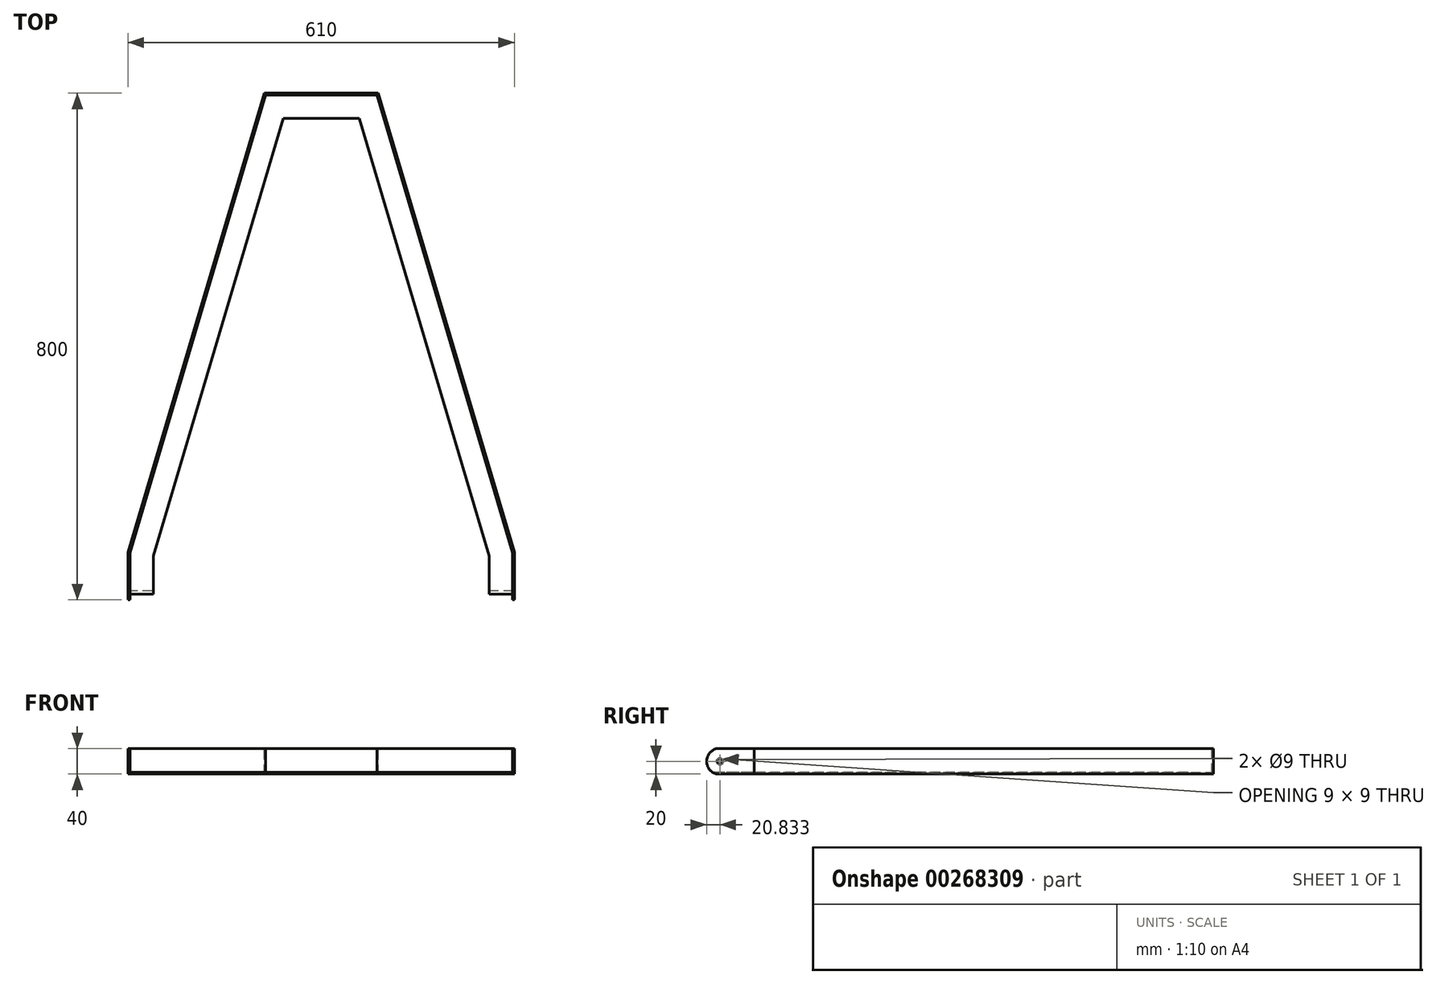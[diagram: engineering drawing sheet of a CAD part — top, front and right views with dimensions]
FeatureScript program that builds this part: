
annotation { "Feature Type Name" : "Feature", "Feature Type Description" : "" }
export const myFeature = defineFeature(function(context is Context, id is Id, definition is map)
    precondition{}
    {
        {
            var Q0;
            Q0=qCreatedBy(makeId("Top.planeOp"),FACE);
            var sketch = newSketch(context, id + "F0", { "sketchPlane" : qUnion([Q0])});
            skLineSegment(sketch, "E0", {"start": v(305, 0) * mm, "end": v(305, 75) * mm});
            skLineSegment(sketch, "E1", {"start": v(305, 75) * mm, "end": v(90, 800) * mm});
            skLineSegment(sketch, "E2", {"start": v(90, 800) * mm, "end": v(0, 800) * mm});
            skLineSegment(sketch, "E3.MirrorCS", {"start": v(-90, 800) * mm, "end": v(0, 800) * mm});
            skLineSegment(sketch, "E4.MirrorCS", {"start": v(-305, 75) * mm, "end": v(-90, 800) * mm});
            skLineSegment(sketch, "E5.MirrorCS", {"start": v(-305, 0) * mm, "end": v(-305, 75) * mm});
            skSolve(sketch);
        }
        {
            var Q0;
            Q0=qCreatedBy(makeId("Front.planeOp"),FACE);
            var sketch = newSketch(context, id + "F1", { "sketchPlane" : qUnion([Q0])});
            skLineSegment(sketch, "E6", {"start": v(305, 0) * mm, "end": v(305, 40) * mm});
            skLineSegment(sketch, "E7", {"start": v(305, 40) * mm, "end": v(302, 40) * mm});
            skLineSegment(sketch, "E8", {"start": v(302, 40) * mm, "end": v(302, 3) * mm});
            skLineSegment(sketch, "E9", {"start": v(302, 3) * mm, "end": v(265, 3) * mm});
            skLineSegment(sketch, "E10", {"start": v(265, 3) * mm, "end": v(265, 0) * mm});
            skLineSegment(sketch, "E11", {"start": v(265, 0) * mm, "end": v(305, 0) * mm});
            skSolve(sketch);
        }
        {
            var Q0;
            Q0=makeQuery(id+"F1.imprint","IMPRINT",FACE,{"disambiguationData":[TD([[makeQuery(id+"F1.imprint","IMPRINT",EDGE,{"derivedFrom":sQuery(id+"F1.wireOp",EDGE,"E6")}),1.0]])]});
            var Q1;
            Q1=sQuery(id+"F0.wireOp",EDGE,"E0");
            var Q2;
            Q2=sQuery(id+"F0.wireOp",EDGE,"E1");
            var Q3;
            Q3=sQuery(id+"F0.wireOp",EDGE,"E2");
            var Q4;
            Q4=sQuery(id+"F0.wireOp",EDGE,"E3.MirrorCS");
            var Q5;
            Q5=sQuery(id+"F0.wireOp",EDGE,"E4.MirrorCS");
            var Q6;
            Q6=sQuery(id+"F0.wireOp",EDGE,"E5.MirrorCS");
            sweep(context, id + "F2", {"profiles" : qUnion([Q0]), "path" : qUnion([Q1, Q2, Q3, Q4, Q5, Q6])});
        }
        {
            var Q0;
            Q0=qCreatedBy(makeId("Right.planeOp"),FACE);
            var sketch = newSketch(context, id + "F3", { "sketchPlane" : qUnion([Q0])});
            skArc(sketch, "E12", {"start": v(15, 40) * mm, "mid": v(0, 20) * mm, "end": v(15, 0) * mm});
            skLineSegment(sketch, "E13", {"start": v(15, 40) * mm, "end": v(0, 40) * mm});
            skLineSegment(sketch, "E14", {"start": v(0, 40) * mm, "end": v(0, 0) * mm});
            skLineSegment(sketch, "E15", {"start": v(0, 0) * mm, "end": v(15, 0) * mm});
            skSolve(sketch);
        }
        {
            var Q0;
            Q0 = qSketchRegion(id + "F3", true);
            extrude(context, id + "F4", {"entities" : qUnion([Q0]), "operationType" : NewBodyOperationType.REMOVE, "endBound" : BoundingType.THROUGH_ALL, "oppositeDirection" : true, "depth" : 25 * mm, "hasSecondDirection" : true, "secondDirectionBound" : SecondDirectionBoundingType.THROUGH_ALL, "secondDirectionOppositeDirection" : false, "secondDirectionDepth" : 25 * mm});
        }
        {
            var Q0;
            Q0=qCreatedBy(makeId("Right.planeOp"),FACE);
            var sketch = newSketch(context, id + "F5", { "sketchPlane" : qUnion([Q0])});
            skArc(sketch, "E16.0", {"start": v(15, 40) * mm, "mid": v(0, 20) * mm, "end": v(15, 0) * mm});
            skSolve(sketch);
        }
        {
            var Q0;
            Q0=sQuery(id+"F5.wireOp",VERTEX,"E16.0.center");
            var Q1;
            Q1=makeQuery(id+"F2.opSweep","SWEPT_BODY",BODY,{"disambiguationData":[OSD([sQuery(id+"F0.wireOp",EDGE,"E5.MirrorCS"),sQuery(id+"F1.wireOp",EDGE,"E6"),sQuery(id+"F1.wireOp",EDGE,"E7"),sQuery(id+"F1.wireOp",EDGE,"E8"),sQuery(id+"F1.wireOp",EDGE,"E9"),sQuery(id+"F1.wireOp",EDGE,"E10"),sQuery(id+"F1.wireOp",EDGE,"E11")])]});
            hole(context, id + "F6", {"style" : HoleStyle.SIMPLE, "endStyle" : HoleEndStyle.THROUGH, "holeDiameter" : 9 * mm, "tappedDepth" : 12 * mm, "tapClearance" : 3, "locations" : qUnion([Q0]), "scope" : qUnion([Q1])});
        }
        {
            var Q0;
            Q0=qCreatedBy(makeId("Right.planeOp"),FACE);
            var sketch = newSketch(context, id + "F7", { "sketchPlane" : qUnion([Q0])});
            skArc(sketch, "E17.0", {"start": v(15, 40) * mm, "mid": v(0, 20) * mm, "end": v(15, 0) * mm});
            skSolve(sketch);
        }
        {
            var Q0;
            Q0=sQuery(id+"F7.wireOp",VERTEX,"E17.0.center");
            var Q1;
            Q1=makeQuery(id+"F2.opSweep","SWEPT_BODY",BODY,{"disambiguationData":[OSD([sQuery(id+"F0.wireOp",EDGE,"E5.MirrorCS"),sQuery(id+"F1.wireOp",EDGE,"E6"),sQuery(id+"F1.wireOp",EDGE,"E7"),sQuery(id+"F1.wireOp",EDGE,"E8"),sQuery(id+"F1.wireOp",EDGE,"E9"),sQuery(id+"F1.wireOp",EDGE,"E10"),sQuery(id+"F1.wireOp",EDGE,"E11")])]});
            hole(context, id + "F8", {"style" : HoleStyle.SIMPLE, "endStyle" : HoleEndStyle.THROUGH, "oppositeDirection" : true, "holeDiameter" : 9 * mm, "tappedDepth" : 12 * mm, "tapClearance" : 3, "locations" : qUnion([Q0]), "scope" : qUnion([Q1])});
        }
    });
